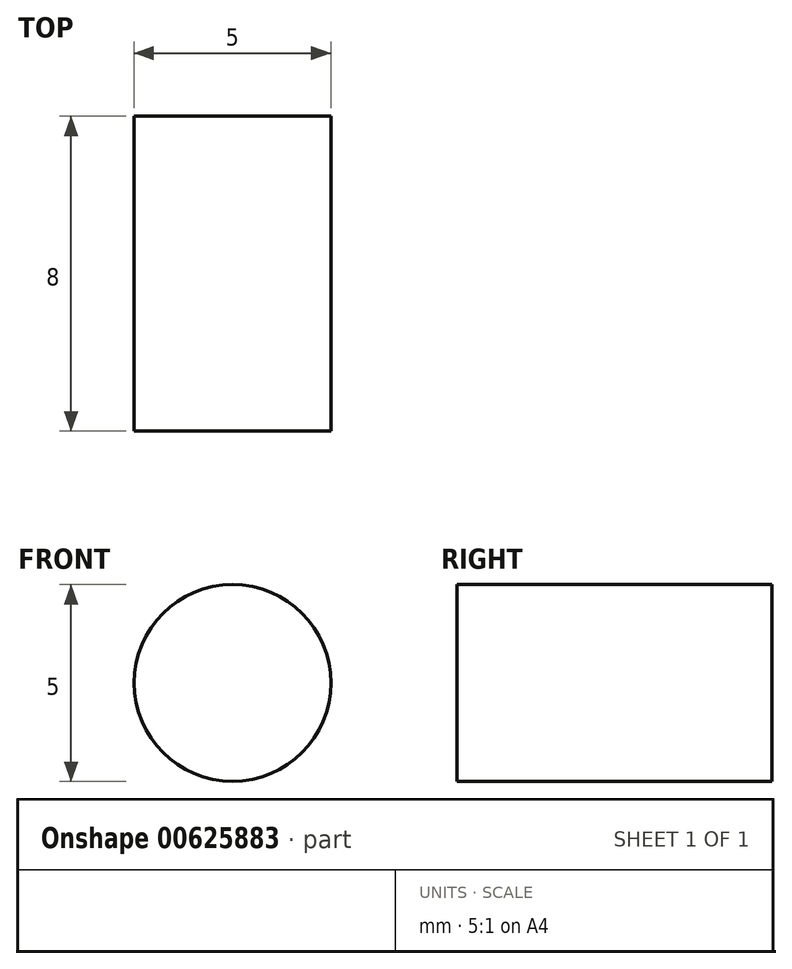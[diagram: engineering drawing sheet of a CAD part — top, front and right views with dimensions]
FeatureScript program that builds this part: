
annotation { "Feature Type Name" : "Feature", "Feature Type Description" : "" }
export const myFeature = defineFeature(function(context is Context, id is Id, definition is map)
    precondition{}
    {
        {
            var Q0;
            Q0=qCreatedBy(makeId("Front.planeOp"),FACE);
            var sketch = newSketch(context, id + "F0", { "sketchPlane" : qUnion([Q0])});
            skCircle(sketch, "E0", {"center": v(0, 0) * mm, "radius": 2.5 * mm});
            skSolve(sketch);
        }
        {
            var Q0;
            Q0=makeQuery(id+"F0.imprint","IMPRINT",FACE,{"disambiguationData":[TD([[makeQuery(id+"F0.imprint","IMPRINT",EDGE,{"derivedFrom":sQuery(id+"F0.wireOp",EDGE,"E0")}),1.0]])]});
            extrude(context, id + "F1", {"entities" : qUnion([Q0]), "depth" : 8 * mm, "offsetDistance" : 25 * mm});
        }
    });
